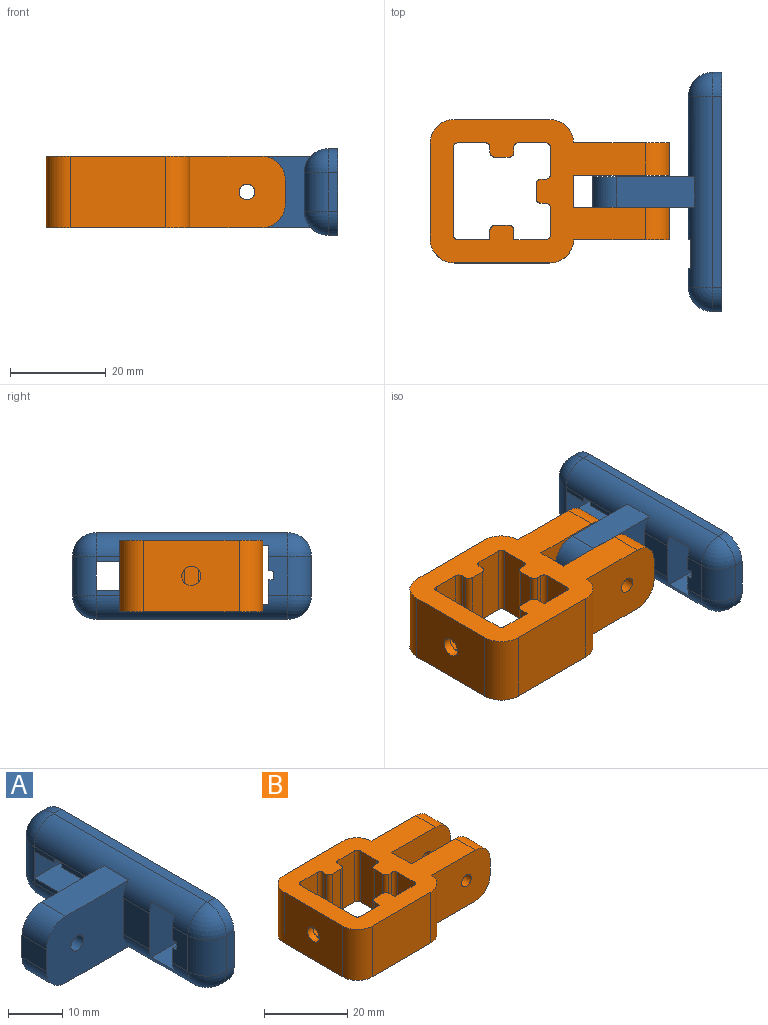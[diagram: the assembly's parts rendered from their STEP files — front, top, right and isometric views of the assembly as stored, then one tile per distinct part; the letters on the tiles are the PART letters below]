
ASSEMBLY  parts=2 mates=1
PART A: 49 faces, bbox 27x50x18.1 mm
  f0: plane 8.13x6.8mm, normal (-1,0,0), area 55.3mm2, adj f7,f32,f39,f48
  f1: plane 16.8x8.13mm, normal (-1,0,0), area 54.7mm2, adj f5,f18,f19,f21,f22,f24,f39,f45
  f2: plane 8.13x4mm, normal (-1,0,0), area 30.5mm2, adj f26,f27,f28,f29,f30,f35,f36,f39
  f3: plane 16.37x6.4mm, normal (0,0,1), area 104.8mm2, adj f5,f7,f10,f39
  f4: plane 16.37x6.4mm, normal (0,0,-1), area 104.8mm2, adj f5,f7,f9,f48
  f5: plane 21.37x15mm, normal (0,1,0), area 283.7mm2, adj f1,f3,f4,f6,f8,f9,f10,f39
  f6: plane 6.4x5mm, normal (-1,0,0), area 32mm2, adj f5,f7,f9,f10
  f7: plane 21.37x15mm, normal (0,-1,0), area 283.7mm2, adj f0,f3,f4,f6,f8,f9,f10,f39
  f8: cylinder r=1.65mm len=6.4mm, axis (0,-1,0), area 66.4mm2, adj f5,f7
  f9: cylinder r=5mm len=6.4mm, axis (0,-1,0), area 50.3mm2, adj f4,f5,f6,f7
  f10: cylinder r=5mm len=6.4mm, axis (0,1,0), area 50.3mm2, adj f3,f5,f6,f7
  f11: plane 5.58x1.06mm, normal (-1,0,0), area 5.6mm2, adj f15,f16,f23,f39,f45
  f12: plane 8.13x2mm, normal (0,1,0), area 16.3mm2, adj f14,f38,f44,f45
  f13: plane 8.13x2mm, normal (0,-1,0), area 16.3mm2, adj f14,f37,f42,f43
  f14: plane 50x18.13mm, normal (1,0,0), area 732.3mm2, adj f12,f13,f15,f16,f17,f18,f19,f20
  f15: plane 7x5.24mm, normal (0,0,-1), area 36.7mm2, adj f11,f14,f16,f20
  f16: plane 7x0.59mm, normal (0,-1,0), area 4.1mm2, adj f11,f14,f15,f23
  f17: plane 7x0.9mm, normal (0,0,-1), area 6.3mm2, adj f14,f23,f24,f39
  f18: plane 7x0.59mm, normal (0,1,0), area 4.1mm2, adj f1,f14,f19,f24
  f19: plane 7x5.24mm, normal (0,0,-1), area 36.7mm2, adj f1,f14,f18,f21
  f20: plane 7x6mm, normal (0,-1,0), area 42mm2, adj f14,f15,f22,f45
  f21: plane 7x6mm, normal (0,1,0), area 42mm2, adj f1,f14,f19,f22
  f22: plane 12.38x7mm, normal (0,0,1), area 86.7mm2, adj f1,f14,f20,f21
  f23: cylinder r=0.5mm len=7mm, axis (1,0,0), area 5.5mm2, adj f11,f14,f16,f17,f39
  f24: cylinder r=0.5mm len=7mm, axis (-1,0,0), area 5.5mm2, adj f1,f14,f17,f18,f39
  f25: plane 6.46x6mm, normal (0,0,-1), area 38.8mm2, adj f14,f26,f32,f39
  f26: plane 7x5.24mm, normal (0,1,0), area 36.3mm2, adj f2,f14,f25,f27,f39
  f27: plane 7x0.59mm, normal (0,0,-1), area 4.1mm2, adj f2,f14,f26,f35
  f28: plane 7x0.9mm, normal (0,1,0), area 6.3mm2, adj f2,f14,f35,f36
  f29: plane 7x0.59mm, normal (0,0,1), area 4.1mm2, adj f2,f14,f30,f36
  f30: plane 7x5.24mm, normal (0,1,0), area 36.4mm2, adj f2,f14,f29,f31,f48
  f31: plane 6.58x6mm, normal (0,0,1), area 39.5mm2, adj f14,f30,f32,f48
  f32: plane 12.38x7mm, normal (0,-1,0), area 86mm2, adj f0,f14,f25,f31,f39,f48
  f33: plane 40x2mm, normal (0,0,-1), area 80mm2, adj f14,f43,f44,f48
  f34: plane 40x2mm, normal (0,0,1), area 80mm2, adj f14,f37,f38,f39
  f35: cylinder r=0.5mm len=7mm, axis (1,0,0), area 5.5mm2, adj f2,f14,f27,f28
  f36: cylinder r=0.5mm len=7mm, axis (-1,0,0), area 5.5mm2, adj f2,f14,f28,f29
  f37: cylinder r=5mm len=5mm, axis (1,0,0), area 15.7mm2, adj f13,f14,f34,f40
  f38: cylinder r=5mm len=5mm, axis (-1,0,0), area 15.7mm2, adj f12,f14,f34,f41
  f39: cylinder r=5mm len=40mm, axis (0,-1,0), area 275.8mm2, adj f0,f1,f2,f3,f5,f7,f11,f17
  f40: sphere r=5mm, area 39.3mm2, adj f37,f39,f42
  f41: sphere r=5mm, area 39.3mm2, adj f38,f39,f45
  f42: cylinder r=5mm len=8.13mm, axis (0,0,-1), area 63.8mm2, adj f2,f13,f40,f46
  f43: cylinder r=5mm len=5mm, axis (-1,0,0), area 15.7mm2, adj f13,f14,f33,f46
  f44: cylinder r=5mm len=5mm, axis (1,0,0), area 15.7mm2, adj f12,f14,f33,f47
  f45: cylinder r=5mm len=8.13mm, axis (0,0,1), area 63.8mm2, adj f1,f11,f12,f20,f41,f47
  f46: sphere r=5mm, area 39.3mm2, adj f42,f43,f48
  f47: sphere r=5mm, area 39.3mm2, adj f44,f45,f48
  f48: cylinder r=5mm len=40mm, axis (0,1,0), area 277.6mm2, adj f0,f1,f2,f4,f5,f7,f30,f31
PART B: 60 faces, bbox 50x30x15 mm
  f0: plane 15x6.7mm, normal (1,0,0), area 100.5mm2, adj f11,f12,f45,f49
  f1: plane 15x5.65mm, normal (-1,0,0), area 84.8mm2, adj f11,f12,f23,f35
  f2: plane 15x6.65mm, normal (0,1,0), area 99.7mm2, adj f11,f12,f16,f33
  f3: plane 15x5.65mm, normal (0,-1,0), area 84.8mm2, adj f11,f12,f29,f34
  f4: plane 20x15mm, normal (0,1,0), area 300mm2, adj f11,f12,f56,f59
  f5: plane 20x15mm, normal (-1,0,0), area 287.4mm2, adj f11,f12,f43,f57,f59
  f6: plane 20x15mm, normal (0,-1,0), area 300mm2, adj f11,f12,f57,f58
  f7: plane 15x5.65mm, normal (-1,0,0), area 84.8mm2, adj f11,f12,f22,f32
  f8: plane 15x6.65mm, normal (0,1,0), area 99.7mm2, adj f11,f12,f18,f32
  f9: plane 18.3x15mm, normal (1,0,0), area 243.3mm2, adj f11,f12,f33,f34,f36,f37,f38,f39
  f10: plane 15x5.65mm, normal (0,-1,0), area 84.8mm2, adj f11,f12,f28,f35
  f11: plane 45x30mm, normal (0,0,1), area 715.9mm2, adj f0,f1,f2,f3,f4,f5,f6,f7
  f12: plane 45x30mm, normal (0,0,-1), area 715.9mm2, adj f0,f1,f2,f3,f4,f5,f6,f7
  f13: plane 15x1mm, normal (1,0,0), area 15mm2, adj f11,f12,f28,f30
  f14: plane 15x1mm, normal (-1,0,0), area 15mm2, adj f11,f12,f29,f31
  f15: plane 15x3mm, normal (0,-1,0), area 45mm2, adj f11,f12,f30,f31
  f16: plane 15x2mm, normal (-1,0,0), area 30mm2, adj f2,f11,f12,f26
  f17: plane 15x3mm, normal (0,1,0), area 45mm2, adj f11,f12,f26,f27
  f18: plane 15x2mm, normal (1,0,0), area 30mm2, adj f8,f11,f12,f27
  f19: plane 15x1mm, normal (0,-1,0), area 15mm2, adj f11,f12,f22,f24
  f20: plane 15x1mm, normal (0,1,0), area 15mm2, adj f11,f12,f23,f25
  f21: plane 15x3mm, normal (-1,0,0), area 45mm2, adj f11,f12,f24,f25
  f22: cylinder r=1mm len=15mm, axis (0,0,1), area 23.6mm2, adj f7,f11,f12,f19
  f23: cylinder r=1mm len=15mm, axis (0,0,-1), area 23.6mm2, adj f1,f11,f12,f20
  f24: cylinder r=1mm len=15mm, axis (0,0,1), area 23.6mm2, adj f11,f12,f19,f21
  f25: cylinder r=1mm len=15mm, axis (0,0,-1), area 23.6mm2, adj f11,f12,f20,f21
  f26: cylinder r=1mm len=15mm, axis (0,0,-1), area 23.6mm2, adj f11,f12,f16,f17
  f27: cylinder r=1mm len=15mm, axis (0,0,1), area 23.6mm2, adj f11,f12,f17,f18
  f28: cylinder r=1mm len=15mm, axis (0,0,1), area 23.6mm2, adj f10,f11,f12,f13
  f29: cylinder r=1mm len=15mm, axis (0,0,-1), area 23.6mm2, adj f3,f11,f12,f14
  f30: cylinder r=1mm len=15mm, axis (0,0,1), area 23.6mm2, adj f11,f12,f13,f15
  f31: cylinder r=1mm len=15mm, axis (0,0,-1), area 23.6mm2, adj f11,f12,f14,f15
  f32: cylinder r=1mm len=15mm, axis (0,0,-1), area 23.6mm2, adj f7,f8,f11,f12
  f33: cylinder r=1mm len=15mm, axis (0,0,1), area 23.6mm2, adj f2,f9,f11,f12
  f34: cylinder r=1mm len=15mm, axis (0,0,-1), area 23.6mm2, adj f3,f9,f11,f12
  f35: cylinder r=1mm len=15mm, axis (0,0,1), area 23.6mm2, adj f1,f10,f11,f12
  f36: plane 3x3mm, normal (0,0.87,0.5), area 10.4mm2, adj f9,f37,f41,f42
  f37: plane 3.46x3mm, normal (0,0,1), area 10.4mm2, adj f9,f36,f38,f42
  f38: plane 3x3mm, normal (0,-0.87,0.5), area 10.4mm2, adj f9,f37,f39,f42
  f39: plane 3x3mm, normal (0,-0.87,-0.5), area 10.4mm2, adj f9,f38,f40,f42
  f40: plane 3.46x3mm, normal (0,0,-1), area 10.4mm2, adj f9,f39,f41,f42
  f41: plane 3x3mm, normal (0,0.87,-0.5), area 10.4mm2, adj f9,f36,f40,f42
  f42: plane 6.93x6mm, normal (1,0,0), area 18.6mm2, adj f36,f37,f38,f39,f40,f41,f43
  f43: cylinder r=2mm len=4mm, axis (1,0,0), area 23.2mm2, adj f5,f42
  f44: plane 20x15mm, normal (0,1,0), area 280.7mm2, adj f11,f12,f46,f51,f54,f55,f56
  f45: plane 20x15mm, normal (0,-1,0), area 280.7mm2, adj f0,f11,f12,f46,f51,f54,f55
  f46: plane 6.8x5mm, normal (1,0,0), area 34mm2, adj f44,f45,f54,f55
  f47: plane 20x15mm, normal (0,-1,0), area 280.7mm2, adj f11,f12,f48,f50,f52,f53,f58
  f48: plane 6.8x5mm, normal (1,0,0), area 34mm2, adj f47,f49,f52,f53
  f49: plane 20x15mm, normal (0,1,0), area 280.7mm2, adj f0,f11,f12,f48,f50,f52,f53
  f50: cylinder r=1.65mm len=6.8mm, axis (0,-1,0), area 70.5mm2, adj f47,f49
  f51: cylinder r=1.65mm len=6.8mm, axis (0,-1,0), area 70.5mm2, adj f44,f45
  f52: cylinder r=5mm len=6.8mm, axis (0,1,0), area 53.4mm2, adj f12,f47,f48,f49
  f53: cylinder r=5mm len=6.8mm, axis (0,1,0), area 53.4mm2, adj f11,f47,f48,f49
  f54: cylinder r=5mm len=6.8mm, axis (0,1,0), area 53.4mm2, adj f12,f44,f45,f46
  f55: cylinder r=5mm len=6.8mm, axis (0,1,0), area 53.4mm2, adj f11,f44,f45,f46
  f56: cylinder r=5mm len=15mm, axis (0,0,1), area 115.6mm2, adj f4,f11,f12,f44
  f57: cylinder r=5mm len=15mm, axis (0,0,-1), area 117.8mm2, adj f5,f6,f11,f12
  f58: cylinder r=5mm len=15mm, axis (0,0,1), area 115.6mm2, adj f6,f11,f12,f47
  f59: cylinder r=5mm len=15mm, axis (0,0,-1), area 117.8mm2, adj f4,f5,f11,f12
PLACE A t=(16.46,2.11,-0.84)mm
PLACE B t=(-12.54,2.26,-0.84)mm
MATE revolute A.f8 <-> B.f50  axis (0,-1,0) through (14.46,-1.09,6.66)mm
